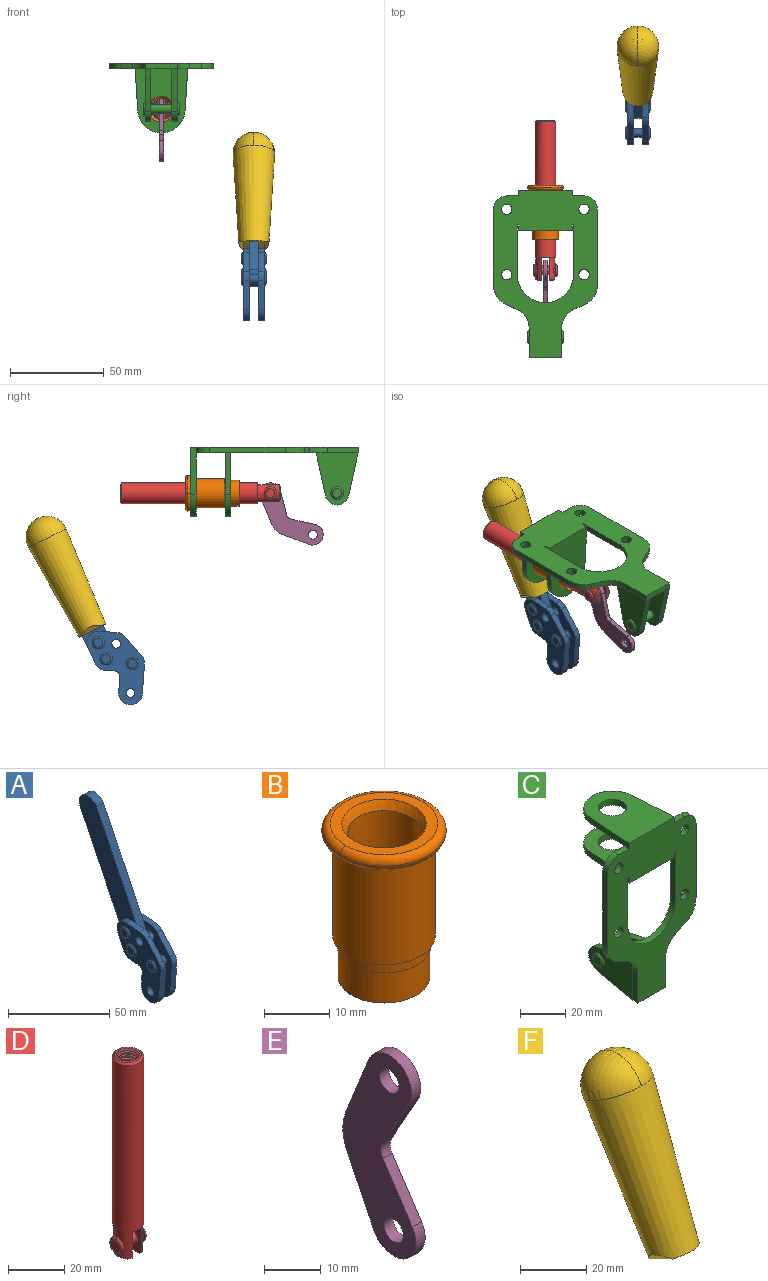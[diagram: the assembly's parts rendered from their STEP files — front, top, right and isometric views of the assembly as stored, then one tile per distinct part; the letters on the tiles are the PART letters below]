
ASSEMBLY  parts=6 mates=4
PART A: 59 faces, bbox 12.9x60.2x99.6 mm
  f0: torus R=2.39mm, axis (-1,0,0), area 14.9mm2, adj f20,f43,f51
  f1: torus R=2.39mm, axis (-1,0,0), area 14.9mm2, adj f19,f42,f51
  f2: torus R=2.39mm, axis (-1,0,0), area 14.9mm2, adj f18,f35,f51
  f3: torus R=2.39mm, axis (-1,0,0), area 14.9mm2, adj f14,f17,f23
  f4: torus R=2.39mm, axis (-1,0,0), area 14.9mm2, adj f13,f16,f23
  f5: torus R=2.39mm, axis (-1,0,0), area 14.9mm2, adj f12,f15,f23
  f6: cylinder r=2.39mm len=4.78mm, axis (1,0,0), area 46.5mm2, adj f48,f50,f51
  f7: cylinder r=2.39mm len=4.78mm, axis (1,0,0), area 46.5mm2, adj f50,f51
  f8: cylinder r=6.35mm len=12.68mm, axis (1,0,0), area 61.8mm2, adj f38,f39,f50,f51
  f9: cylinder r=2.39mm len=4.78mm, axis (-1,0,0), area 70.5mm2, adj f46,f50
  f10: cylinder r=2.39mm len=4.78mm, axis (-1,0,0), area 46.5mm2, adj f23,f45,f46
  f11: cylinder r=2.39mm len=4.78mm, axis (-1,0,0), area 46.5mm2, adj f23,f46
  f12: plane 4.78x4.78mm, normal (1,0,0), area 17.9mm2, adj f5,f15
  f13: plane 4.78x4.78mm, normal (1,0,0), area 17.9mm2, adj f4,f16
  f14: plane 4.78x4.78mm, normal (1,0,0), area 17.9mm2, adj f3,f17
  f15: torus R=2.39mm, axis (-1,0,0), area 14.9mm2, adj f5,f12,f23
  f16: torus R=2.39mm, axis (-1,0,0), area 14.9mm2, adj f4,f13,f23
  f17: torus R=2.39mm, axis (-1,0,0), area 14.9mm2, adj f3,f14,f23
  f18: plane 4.78x4.78mm, normal (-1,0,0), area 17.9mm2, adj f2,f35
  f19: plane 4.78x4.78mm, normal (-1,0,0), area 17.9mm2, adj f1,f42
  f20: plane 4.78x4.78mm, normal (-1,0,0), area 17.9mm2, adj f0,f43
  f21: plane 2.26x0.2mm, normal (1,0,0), area 0.2mm2, adj f31,f44
  f22: plane 2.26x0.2mm, normal (-1,0,0), area 0.2mm2, adj f41,f44
  f23: plane 39.37x30.77mm, normal (1,0,0), area 565.5mm2, adj f3,f4,f5,f10,f11,f15,f16,f17
  f24: cylinder r=6.1mm len=4.15mm, axis (-1,0,0), area 14.7mm2, adj f23,f25,f32,f46
  f25: plane 10.25x9.01mm, normal (0,-0.75,0.66), area 42.3mm2, adj f23,f24,f26,f46
  f26: cylinder r=6.35mm len=4.64mm, axis (-1,0,0), area 15.6mm2, adj f23,f25,f27,f46
  f27: plane 15.84x3.1mm, normal (0,-1,-0.07), area 49.2mm2, adj f23,f26,f28,f46
  f28: cylinder r=6.35mm len=12.68mm, axis (-1,0,0), area 61.8mm2, adj f23,f27,f29,f46
  f29: plane 8.11x3.1mm, normal (0,1,0.07), area 25.2mm2, adj f23,f28,f30,f46
  f30: cylinder r=3.05mm len=3.25mm, axis (-1,0,0), area 14.8mm2, adj f23,f29,f31,f46
  f31: plane 5.99x3.1mm, normal (0,0.07,-1), area 18.6mm2, adj f21,f23,f30,f44,f46
  f32: plane 9.5x3.1mm, normal (0,-0.07,1), area 29.5mm2, adj f23,f24,f33,f46,f47
  f33: cylinder r=6.1mm len=8.63mm, axis (-1,0,0), area 39.1mm2, adj f23,f32,f34,f47
  f34: plane 8.65x3.96mm, normal (0,0.91,-0.42), area 29.5mm2, adj f23,f33,f44,f47
  f35: torus R=2.39mm, axis (-1,0,0), area 14.9mm2, adj f2,f18,f51
  f36: plane 10.25x9.01mm, normal (0,-0.75,0.66), area 42.3mm2, adj f37,f49,f50,f51
  f37: cylinder r=6.35mm len=4.64mm, axis (1,0,0), area 15.6mm2, adj f36,f38,f50,f51
  f38: plane 15.84x3.1mm, normal (0,-1,-0.07), area 49.2mm2, adj f8,f37,f50,f51
  f39: plane 8.11x3.1mm, normal (0,1,0.07), area 25.2mm2, adj f8,f40,f50,f51
  f40: cylinder r=3.05mm len=3.25mm, axis (1,0,0), area 14.8mm2, adj f39,f41,f50,f51
  f41: plane 5.99x3.1mm, normal (0,0.07,-1), area 18.6mm2, adj f22,f40,f44,f50,f51
  f42: torus R=2.39mm, axis (-1,0,0), area 14.9mm2, adj f1,f19,f51
  f43: torus R=2.39mm, axis (-1,0,0), area 14.9mm2, adj f0,f20,f51
  f44: cylinder r=6.35mm len=12.12mm, axis (-1,0,0), area 128.9mm2, adj f21,f22,f23,f31,f34,f41,f46,f47
  f45: plane 2.65x1.35mm, normal (1,0,0), area 1mm2, adj f10,f55
  f46: plane 39.08x20.42mm, normal (-1,0,0), area 412.5mm2, adj f9,f10,f11,f24,f25,f26,f27,f28
  f47: plane 77.62x39.82mm, normal (1,0,0), area 850mm2, adj f32,f33,f34,f44,f53,f54,f55
  f48: plane 2.65x1.35mm, normal (-1,0,0), area 1mm2, adj f6,f55
  f49: cylinder r=6.1mm len=4.15mm, axis (1,0,0), area 14.7mm2, adj f36,f50,f51,f56
  f50: plane 39.08x20.42mm, normal (1,0,0), area 412.5mm2, adj f6,f7,f8,f9,f36,f37,f38,f39
  f51: plane 39.37x30.77mm, normal (-1,0,0), area 565.5mm2, adj f0,f1,f2,f6,f7,f8,f35,f36
  f52: plane 8.65x3.96mm, normal (0,0.91,-0.42), area 29.5mm2, adj f44,f51,f57,f58
  f53: plane 68.49x33.4mm, normal (0,0.9,-0.44), area 358.1mm2, adj f44,f47,f54,f58
  f54: cylinder r=6.35mm len=12.06mm, axis (1,0,0), area 93.7mm2, adj f47,f53,f55,f58
  f55: plane 68.49x33.4mm, normal (0,-0.9,0.44), area 358.1mm2, adj f44,f45,f46,f47,f48,f50,f54,f58
  f56: plane 9.5x3.1mm, normal (0,-0.07,1), area 29.5mm2, adj f49,f50,f51,f57,f58
  f57: cylinder r=6.1mm len=8.63mm, axis (1,0,0), area 39.1mm2, adj f51,f52,f56,f58
  f58: plane 77.62x39.82mm, normal (-1,0,0), area 850mm2, adj f44,f52,f53,f54,f55,f56,f57
PART B: 15 faces, bbox 20.6x20.6x28.7 mm
  f0: torus R=8.26mm, axis (0,0,1), area 56.8mm2, adj f1,f10,f12
  f1: torus R=8.26mm, axis (0,0,1), area 56.8mm2, adj f0,f6,f13
  f2: cylinder r=5.59mm len=25.91mm, axis (0,0,1), area 909.6mm2, adj f3,f4
  f3: cone r=6.86mm half-angle=45deg, axis (0,0,-1), area 70.2mm2, adj f2,f14
  f4: cone r=6.47mm half-angle=30deg, axis (0,0,1), area 66.7mm2, adj f2,f13
  f5: cylinder r=7.04mm len=14.07mm, axis (0,0,1), area 252.6mm2, adj f11,f14
  f6: torus R=8.26mm, axis (0,0,1), area 56.8mm2, adj f1,f12,f13
  f7: cylinder r=7.16mm len=14.33mm, axis (0,0,1), area 91.5mm2, adj f9,f11
  f8: cylinder r=7.86mm len=18.42mm, axis (0,0,1), area 909.6mm2, adj f9,f10
  f9: plane 15.72x15.72mm, normal (0,0,-1), area 33mm2, adj f7,f8
  f10: plane 16.51x16.51mm, normal (0,0,-1), area 19.9mm2, adj f0,f8,f12
  f11: plane 14.33x14.33mm, normal (0,0,-1), area 5.7mm2, adj f5,f7
  f12: torus R=8.26mm, axis (0,0,1), area 56.8mm2, adj f0,f6,f10
  f13: plane 16.51x16.51mm, normal (0,0,1), area 82.7mm2, adj f1,f4,f6
  f14: plane 14.07x14.07mm, normal (0,0,-1), area 7.8mm2, adj f3,f5
PART C: 55 faces, bbox 55.7x37.4x89.8 mm
  f0: torus R=2.41mm, axis (-1,0,0), area 15mm2, adj f11,f15,f25
  f1: torus R=2.41mm, axis (-1,0,0), area 15mm2, adj f10,f12,f22
  f2: cylinder r=2.78mm len=5.56mm, axis (0,-1,0), area 54.2mm2, adj f30,f54
  f3: cylinder r=14.99mm len=29.97mm, axis (0,-1,0), area 145.9mm2, adj f30,f49,f53,f54
  f4: cylinder r=2.78mm len=5.56mm, axis (0,-1,0), area 54.2mm2, adj f30,f54
  f5: cylinder r=2.78mm len=5.56mm, axis (0,-1,0), area 54.2mm2, adj f30,f54
  f6: cylinder r=2.78mm len=5.56mm, axis (0,-1,0), area 54.2mm2, adj f30,f54
  f7: cylinder r=6.35mm len=12.7mm, axis (0,0,1), area 123.6mm2, adj f27,f51
  f8: cylinder r=6.35mm len=12.7mm, axis (0,0,-1), area 124.7mm2, adj f21,f35
  f9: cylinder r=2.41mm len=11.18mm, axis (-1,0,0), area 169.4mm2, adj f16,f19
  f10: plane 4.83x4.83mm, normal (1,0,0), area 18.3mm2, adj f1,f12
  f11: plane 4.83x4.83mm, normal (-1,0,0), area 18.3mm2, adj f0,f15
  f12: torus R=2.41mm, axis (-1,0,0), area 15mm2, adj f1,f10,f22
  f13: cylinder r=6.35mm len=12.41mm, axis (1,0,0), area 53.4mm2, adj f18,f19,f22,f23
  f14: cylinder r=6.35mm len=12.41mm, axis (-1,0,0), area 53.4mm2, adj f16,f17,f24,f25
  f15: torus R=2.41mm, axis (-1,0,0), area 15mm2, adj f0,f11,f25
  f16: plane 27.86x22.35mm, normal (1,0,0), area 425.4mm2, adj f9,f14,f17,f24,f30
  f17: plane 22.86x4.97mm, normal (0,0.21,0.98), area 72.5mm2, adj f14,f16,f25,f30
  f18: plane 22.86x4.97mm, normal (0,0.21,0.98), area 72.5mm2, adj f13,f19,f22,f30
  f19: plane 27.86x22.35mm, normal (-1,0,0), area 425.4mm2, adj f9,f13,f18,f23,f30
  f20: cylinder r=12.7mm len=25.35mm, axis (0,0,-1), area 119.8mm2, adj f21,f34,f35,f36
  f21: plane 34.21x28.07mm, normal (0,0,-1), area 702.4mm2, adj f8,f20,f30,f34,f36
  f22: plane 27.96x22.45mm, normal (1,0,0), area 407.2mm2, adj f1,f12,f13,f18,f23,f30,f42,f43
  f23: plane 22.86x4.97mm, normal (0,0.21,-0.98), area 72.5mm2, adj f13,f19,f22,f44
  f24: plane 22.86x4.97mm, normal (0,0.21,-0.98), area 72.5mm2, adj f14,f16,f25,f44
  f25: plane 27.86x22.35mm, normal (-1,0,0), area 407.1mm2, adj f0,f14,f15,f17,f24,f30,f45,f46
  f26: plane 3.1x0.95mm, normal (0,0,-1), area 2.7mm2, adj f30,f49,f50,f54
  f27: plane 34.21x28.07mm, normal (0,0,1), area 702.4mm2, adj f7,f28,f30,f50,f52
  f28: cylinder r=12.7mm len=25.35mm, axis (0,0,1), area 118.8mm2, adj f27,f50,f51,f52
  f29: plane 3.1x0.95mm, normal (0,0,-1), area 2.7mm2, adj f30,f52,f53,f54
  f30: plane 86.54x55.63mm, normal (0,1,0), area 2362.9mm2, adj f2,f3,f4,f5,f6,f16,f17,f18
  f31: plane 40.56x3.1mm, normal (-1,0,0), area 125.7mm2, adj f30,f32,f48,f54
  f32: cylinder r=7.11mm len=7.11mm, axis (0,-1,0), area 34.6mm2, adj f30,f31,f33,f54
  f33: plane 6.67x3.1mm, normal (0,0,1), area 20.4mm2, adj f30,f32,f34,f54
  f34: plane 25.39x3.13mm, normal (-1,0.06,0), area 79.5mm2, adj f20,f21,f33,f35,f54
  f35: plane 37.31x28.45mm, normal (0,0,1), area 789.9mm2, adj f8,f20,f34,f36,f54
  f36: plane 25.39x3.13mm, normal (1,0.06,0), area 79.5mm2, adj f20,f21,f35,f37,f54
  f37: plane 6.67x3.1mm, normal (0,0,1), area 20.4mm2, adj f30,f36,f38,f54
  f38: cylinder r=7.11mm len=7.11mm, axis (0,-1,0), area 34.6mm2, adj f30,f37,f39,f54
  f39: plane 40.56x3.1mm, normal (1,0,0), area 125.7mm2, adj f30,f38,f40,f54
  f40: cylinder r=11.18mm len=10.16mm, axis (0,-1,0), area 39.5mm2, adj f30,f39,f41,f54
  f41: plane 6.09x3.1mm, normal (0.42,0,-0.91), area 20.8mm2, adj f30,f40,f42,f54
  f42: cylinder r=11.18mm len=9.41mm, axis (0,-1,0), area 37.2mm2, adj f22,f30,f41,f43,f54
  f43: plane 16.5x3.1mm, normal (1,0,0), area 51.1mm2, adj f22,f42,f44,f54
  f44: plane 17.37x3.1mm, normal (0,0,-1), area 53.8mm2, adj f23,f24,f30,f43,f45,f54
  f45: plane 16.5x3.1mm, normal (-1,0,0), area 51.1mm2, adj f25,f44,f46,f54
  f46: cylinder r=11.18mm len=9.41mm, axis (0,-1,0), area 37.2mm2, adj f25,f30,f45,f47,f54
  f47: plane 6.09x3.1mm, normal (-0.42,0,-0.91), area 20.8mm2, adj f30,f46,f48,f54
  f48: cylinder r=11.18mm len=10.16mm, axis (0,-1,0), area 39.5mm2, adj f30,f31,f47,f54
  f49: plane 26.54x3.1mm, normal (-1,0,0), area 82.3mm2, adj f3,f26,f30,f54
  f50: plane 25.39x3.1mm, normal (1,0.06,0), area 78.8mm2, adj f26,f27,f28,f51,f54
  f51: plane 37.31x28.45mm, normal (0,0,-1), area 789.9mm2, adj f7,f28,f50,f52,f54
  f52: plane 25.39x3.1mm, normal (-1,0.06,0), area 78.8mm2, adj f27,f28,f29,f51,f54
  f53: plane 26.54x3.1mm, normal (1,0,0), area 82.3mm2, adj f3,f29,f30,f54
  f54: plane 89.66x55.63mm, normal (0,-1,0), area 2678.5mm2, adj f2,f3,f4,f5,f6,f26,f29,f31
PART D: 48 faces, bbox 12.6x11.1x86.1 mm
  f0: torus R=2.41mm, axis (-1,0,0), area 15mm2, adj f30,f32,f34
  f1: torus R=2.41mm, axis (-1,0,0), area 15mm2, adj f29,f31,f33
  f2: cylinder r=5.54mm len=72.39mm, axis (0,0,1), area 2518.5mm2, adj f3,f4,f42,f43
  f3: cone r=5.54mm half-angle=45deg, axis (0,0,1), area 7.6mm2, adj f2,f5,f41
  f4: cone r=5.54mm half-angle=45deg, axis (0,0,-1), area 34.9mm2, adj f2,f39
  f5: cylinder r=5.08mm len=11.48mm, axis (0,0,1), area 108.3mm2, adj f3,f7,f8,f41
  f6: cylinder r=2.41mm len=4.83mm, axis (-1,0,0), area 71.2mm2, adj f40,f41
  f7: cylinder r=2.41mm len=4.83mm, axis (-1,0,0), area 7.6mm2, adj f5,f34
  f8: cone r=5.08mm half-angle=45deg, axis (0,0,1), area 10.6mm2, adj f5,f37,f41
  f9: cone r=3.98mm half-angle=45deg, axis (0,0,1), area 17.6mm2, adj f27,f39,f45,f46,f47
  f10: cylinder r=2.41mm len=4.83mm, axis (-1,0,0), area 7.6mm2, adj f33,f38
  f11: cylinder r=3.2mm len=6.4mm, axis (0,0,1), area 78.4mm2, adj f12,f28,f44,f45,f47
  f12: cylinder r=3.2mm len=6.4mm, axis (0,0,1), area 10.5mm2, adj f11,f13,f45,f47
  f13: cylinder r=3.2mm len=6.4mm, axis (0,0,1), area 10.5mm2, adj f12,f14,f45,f47
  f14: cylinder r=3.2mm len=6.4mm, axis (0,0,1), area 10.5mm2, adj f13,f15,f45,f47
  f15: cylinder r=3.2mm len=6.4mm, axis (0,0,1), area 10.5mm2, adj f14,f16,f45,f47
  f16: cylinder r=3.2mm len=6.4mm, axis (0,0,1), area 10.5mm2, adj f15,f17,f45,f47
  f17: cylinder r=3.2mm len=6.4mm, axis (0,0,1), area 10.5mm2, adj f16,f18,f45,f47
  f18: cylinder r=3.2mm len=6.4mm, axis (0,0,1), area 10.5mm2, adj f17,f19,f45,f47
  f19: cylinder r=3.2mm len=6.4mm, axis (0,0,1), area 10.5mm2, adj f18,f20,f45,f47
  f20: cylinder r=3.2mm len=6.4mm, axis (0,0,1), area 10.5mm2, adj f19,f21,f45,f47
  f21: cylinder r=3.2mm len=6.4mm, axis (0,0,1), area 10.5mm2, adj f20,f22,f45,f47
  f22: cylinder r=3.2mm len=6.4mm, axis (0,0,1), area 10.5mm2, adj f21,f23,f45,f47
  f23: cylinder r=3.2mm len=6.4mm, axis (0,0,1), area 10.5mm2, adj f22,f24,f45,f47
  f24: cylinder r=3.2mm len=6.4mm, axis (0,0,1), area 10.5mm2, adj f23,f25,f45,f47
  f25: cylinder r=3.2mm len=6.4mm, axis (0,0,1), area 10.5mm2, adj f24,f26,f45,f47
  f26: cylinder r=3.2mm len=6.4mm, axis (0,0,1), area 10.5mm2, adj f25,f27,f45,f47
  f27: cylinder r=3.2mm len=6.4mm, axis (0,0,1), area 7.4mm2, adj f9,f26,f45,f47
  f28: cone r=3.2mm half-angle=60deg, axis (0,0,1), area 37.2mm2, adj f11
  f29: plane 4.83x4.83mm, normal (-1,0,0), area 18.3mm2, adj f1,f31
  f30: plane 4.83x4.83mm, normal (1,0,0), area 18.3mm2, adj f0,f32
  f31: torus R=2.41mm, axis (-1,0,0), area 15mm2, adj f1,f29,f33
  f32: torus R=2.41mm, axis (-1,0,0), area 15mm2, adj f0,f30,f34
  f33: plane 6.83x6.83mm, normal (1,0,0), area 18.3mm2, adj f1,f10,f31
  f34: plane 6.83x6.83mm, normal (-1,0,0), area 18.3mm2, adj f0,f7,f32
  f35: cone r=5.08mm half-angle=45deg, axis (0,0,1), area 10.6mm2, adj f36,f38,f40
  f36: plane 7.25x1.97mm, normal (0,0,-1), area 10mm2, adj f35,f40
  f37: plane 7.25x1.97mm, normal (0,0,-1), area 10mm2, adj f8,f41
  f38: cylinder r=5.08mm len=11.48mm, axis (0,0,1), area 108.3mm2, adj f10,f35,f40,f42
  f39: plane 9.55x9.55mm, normal (0,0,1), area 22mm2, adj f4,f9
  f40: plane 12.76x10.09mm, normal (1,0,0), area 95.7mm2, adj f6,f35,f36,f38,f42,f43
  f41: plane 12.76x10.09mm, normal (-1,0,0), area 95.7mm2, adj f3,f5,f6,f8,f37,f43
  f42: cone r=5.54mm half-angle=45deg, axis (0,0,1), area 7.6mm2, adj f2,f38,f40
  f43: plane 11.07x4.7mm, normal (0,0,-1), area 50.4mm2, adj f2,f40,f41
  f44: plane 0.89x0.62mm, normal (-1,0,0), area 0.3mm2, adj f11,f45,f46,f47
  f45: bspline ~24.8x7.63mm, area 266.6mm2, adj f9,f11,f12,f13,f14,f15,f16,f17
  f46: bspline ~24.87x7.63mm, area 73.6mm2, adj f9,f44,f45,f47
  f47: bspline ~24.98x7.63mm, area 272.5mm2, adj f9,f11,f12,f13,f14,f15,f16,f17
PART E: 12 faces, bbox 2.3x18.2x42.8 mm
  f0: cylinder r=2.4mm len=4.8mm, axis (1,0,0), area 34.9mm2, adj f4,f11
  f1: cylinder r=10.41mm len=8.47mm, axis (1,0,0), area 20.2mm2, adj f4,f9,f10,f11
  f2: cylinder r=3.05mm len=3.16mm, axis (1,0,0), area 7.7mm2, adj f4,f6,f7,f11
  f3: cylinder r=2.4mm len=4.8mm, axis (1,0,0), area 34.9mm2, adj f4,f11
  f4: plane 42.81x18.23mm, normal (-1,0,0), area 414.1mm2, adj f0,f1,f2,f3,f5,f6,f7,f8
  f5: cylinder r=5.54mm len=10.67mm, axis (1,0,0), area 41.8mm2, adj f4,f6,f10,f11
  f6: plane 11.66x6.53mm, normal (0,-0.87,-0.49), area 30.9mm2, adj f2,f4,f5,f11
  f7: plane 11.17x7.33mm, normal (0,-0.84,0.55), area 30.9mm2, adj f2,f4,f8,f11
  f8: cylinder r=5.54mm len=10.51mm, axis (1,0,0), area 41.8mm2, adj f4,f7,f9,f11
  f9: plane 13.67x6.67mm, normal (0,0.9,-0.44), area 35.1mm2, adj f1,f4,f8,f11
  f10: plane 14.1x5.7mm, normal (0,0.93,0.37), area 35.1mm2, adj f1,f4,f5,f11
  f11: plane 42.81x18.23mm, normal (1,0,0), area 414.1mm2, adj f0,f1,f2,f3,f5,f6,f7,f8
PART F: 11 faces, bbox 22.3x42.6x64.5 mm
  f0: sphere r=11.13mm, area 411.4mm2, adj f1,f8
  f1: cone r=11.11mm half-angle=3.3deg, axis (0,0.44,0.9), area 3251.8mm2, adj f0,f7,f8,f9,f10
  f2: cylinder r=6.16mm len=11.7mm, axis (1,0,0), area 89.5mm2, adj f3,f4,f5,f6
  f3: plane 60.23x36.75mm, normal (-1,0,0), area 763.6mm2, adj f2,f4,f6,f10
  f4: plane 51.37x25.05mm, normal (0,0.9,-0.44), area 264.2mm2, adj f2,f3,f5,f10
  f5: plane 60.23x36.75mm, normal (1,0,0), area 763.6mm2, adj f2,f4,f6,f10
  f6: plane 51.37x25.05mm, normal (0,-0.9,0.44), area 264.2mm2, adj f2,f3,f5,f10
  f7: plane 9.95x5.95mm, normal (0.71,-0.31,-0.64), area 25.8mm2, adj f1,f10
  f8: sphere r=11.13mm, area 411.4mm2, adj f0,f1
  f9: plane 9.95x5.95mm, normal (-0.71,-0.31,-0.64), area 25.8mm2, adj f1,f10
  f10: plane 14.27x11.38mm, normal (0,-0.44,-0.9), area 106.7mm2, adj f1,f3,f4,f5,f6,f7,f9
PLACE A t=(49.43,52.41,-96.18)mm
PLACE B rot(axis=(-1,0,0),90deg) t=(0,-1.23,3.1)mm
PLACE C rot(axis=(-1,0,0),90deg) t=(0,-1.23,3.1)mm fixed
PLACE D rot(axis=(-1,0,0),90deg) t=(0,-13.17,3.1)mm
PLACE E rot(axis=(-1,0,0),43.7deg) t=(0,-26.18,-15.71)mm
PLACE F t=(49.39,51.4,-98.3)mm
MATE fastened B.f0 <-> C.f7  axis (0,-1,0) through (0,45.16,-21.51)mm
MATE slider A.f58 <-> F.f5  axis (-1,0,0) through (47.08,110.99,-67.02)mm
MATE slider D.f2 <-> B.f2  axis (0,1,0) through (0,45.61,-21.51)mm
MATE revolute E.f5 <-> D.f6  axis (1,0,0) through (0,2.31,-21.51)mm
